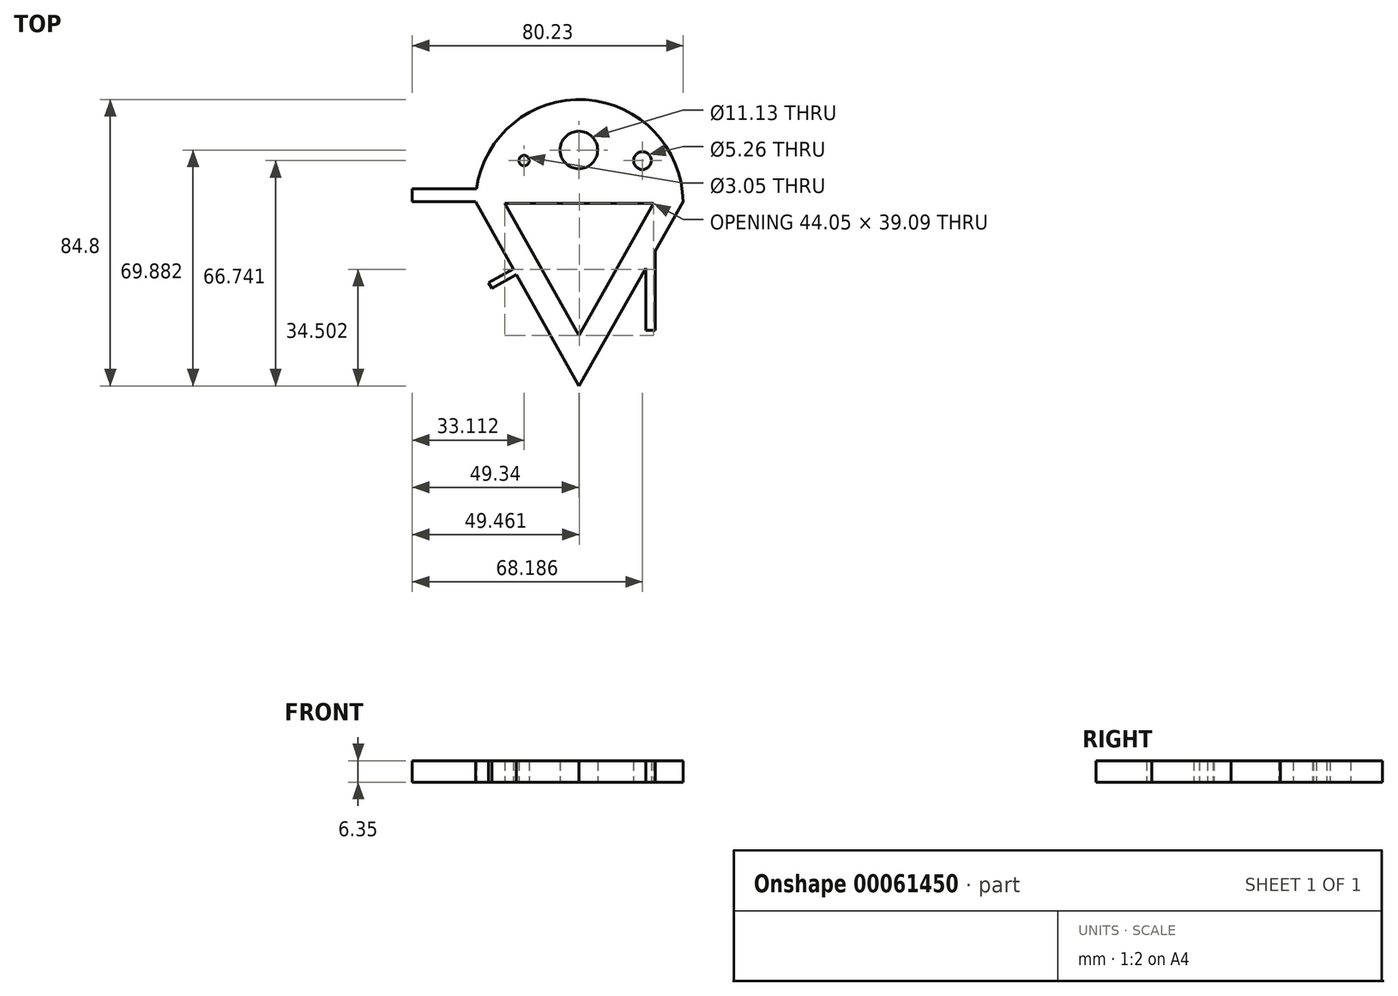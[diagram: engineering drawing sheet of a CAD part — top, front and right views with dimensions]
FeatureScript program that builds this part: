
annotation { "Feature Type Name" : "Feature", "Feature Type Description" : "" }
export const myFeature = defineFeature(function(context is Context, id is Id, definition is map)
    precondition{}
    {
        {
            var Q0;
            Q0=qCreatedBy(makeId("Top.planeOp"),FACE);
            var sketch = newSketch(context, id + "F0", { "sketchPlane" : qUnion([Q0])});
            skLineSegment(sketch, "E0", {"start": v(0, -54.57) * mm, "end": v(30.89, 0) * mm});
            skLineSegment(sketch, "E1", {"start": v(0, -54.57) * mm, "end": v(-30.62, 0) * mm});
            skArc(sketch, "E2", {"start": v(30.89, 0) * mm, "mid": v(0.13, 30.23) * mm, "end": v(-30.62, 0) * mm});
            skLineSegment(sketch, "E3.0", {"start": v(0.03, -39.61) * mm, "end": v(-21.9, -0.53) * mm});
            skLineSegment(sketch, "E3.1", {"start": v(0.03, -39.61) * mm, "end": v(22.15, -0.53) * mm});
            skLineSegment(sketch, "E4", {"start": v(0.13, -0.53) * mm, "end": v(22.15, -0.53) * mm});
            skLineSegment(sketch, "E5", {"start": v(0.13, -0.53) * mm, "end": v(-21.9, -0.53) * mm});
            skCircle(sketch, "E6", {"center": v(0, 15.31) * mm, "radius": 5.56 * mm});
            skCircle(sketch, "E7", {"center": v(18.85, 12.17) * mm, "radius": 2.63 * mm});
            skCircle(sketch, "E8", {"center": v(-16.23, 12.17) * mm, "radius": 1.53 * mm});
            skLineSegment(sketch, "E9", {"start": v(-19.45, -19.92) * mm, "end": v(-26.72, -24) * mm});
            skLineSegment(sketch, "E10", {"start": v(-26.72, -24) * mm, "end": v(-25.8, -25.66) * mm});
            skLineSegment(sketch, "E11", {"start": v(-25.8, -25.66) * mm, "end": v(-18.52, -21.58) * mm});
            skLineSegment(sketch, "E12", {"start": v(-30.33, 3.77) * mm, "end": v(-49.34, 3.77) * mm});
            skLineSegment(sketch, "E13", {"start": v(-49.34, 3.77) * mm, "end": v(-49.34, 0) * mm});
            skLineSegment(sketch, "E14", {"start": v(-49.34, 0) * mm, "end": v(-30.62, 0) * mm});
            skLineSegment(sketch, "E15", {"start": v(19.78, -19.62) * mm, "end": v(19.78, -38.1) * mm});
            skLineSegment(sketch, "E16", {"start": v(19.78, -38.1) * mm, "end": v(22.64, -38.1) * mm});
            skLineSegment(sketch, "E17", {"start": v(22.64, -38.1) * mm, "end": v(22.64, -14.57) * mm});
            skSolve(sketch);
        }
        {
            var Q0;
            Q0 = qSketchRegion(id + "F0", true);
            var Q1;
            Q1 = qSketchRegion(id + "FlNGlofoUCXpoIg_0", true);
            extrude(context, id + "F1", {"entities" : qUnion([Q0, Q1]), "depth" : 6.35 * mm});
        }
    });
